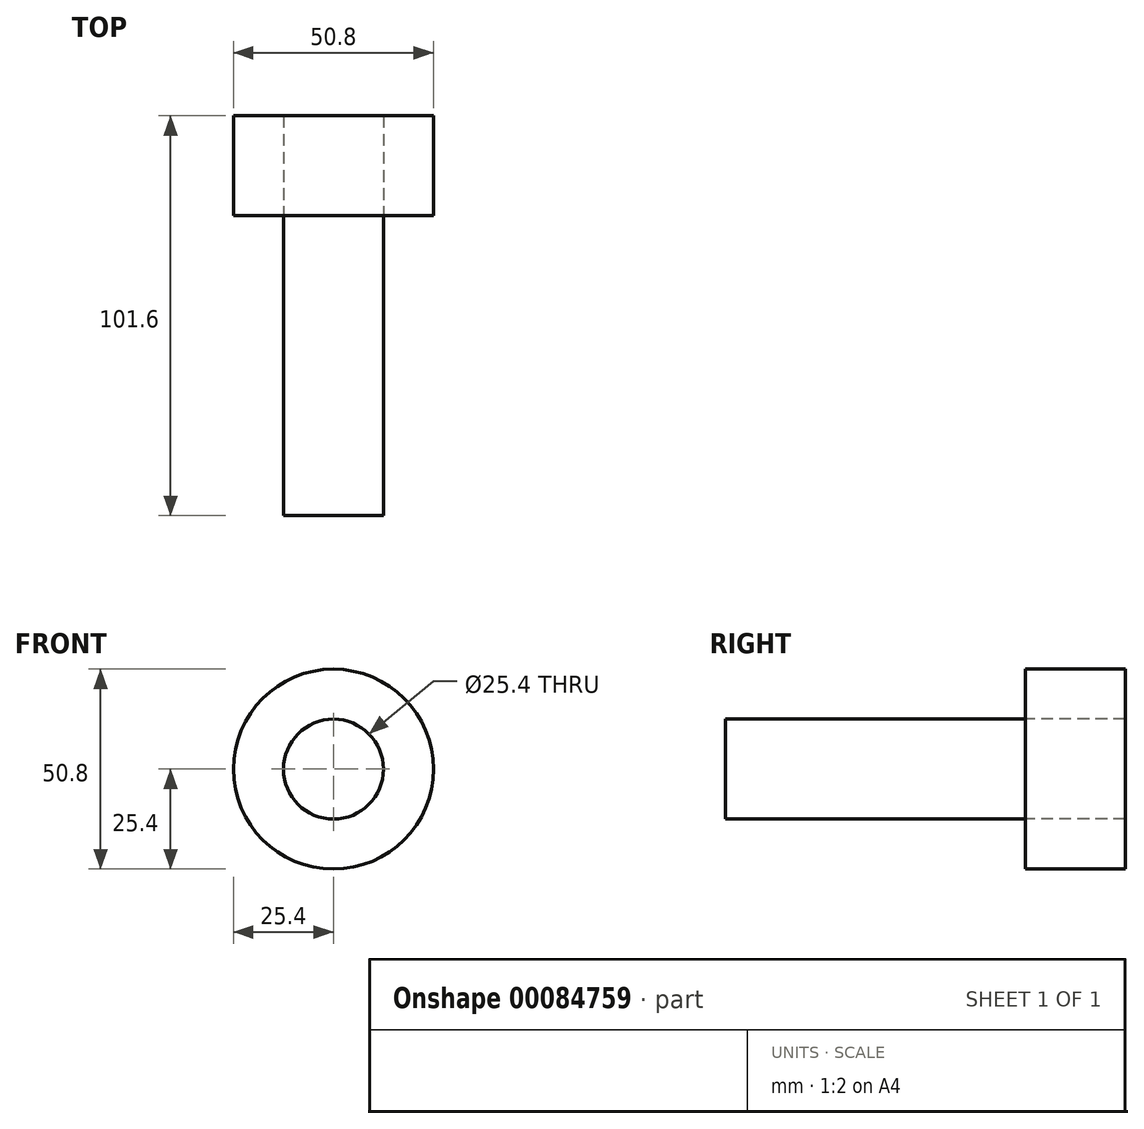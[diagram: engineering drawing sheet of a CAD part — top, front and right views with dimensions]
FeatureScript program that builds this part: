
annotation { "Feature Type Name" : "Feature", "Feature Type Description" : "" }
export const myFeature = defineFeature(function(context is Context, id is Id, definition is map)
    precondition{}
    {
        {
            var Q0;
            Q0=qCreatedBy(makeId("Front.planeOp"),FACE);
            var sketch = newSketch(context, id + "F0", { "sketchPlane" : qUnion([Q0])});
            skCircle(sketch, "E0", {"center": v(0, 0) * mm, "radius": 12.7 * mm});
            skCircle(sketch, "E1", {"center": v(0, 0) * mm, "radius": 25.4 * mm});
            skSolve(sketch);
        }
        {
            var Q0;
            Q0=makeQuery(id+"F0.imprint","IMPRINT",FACE,{"disambiguationData":[TD([[makeQuery(id+"F0.imprint","IMPRINT",EDGE,{"derivedFrom":sQuery(id+"F0.wireOp",EDGE,"E0")}),1.0]])]});
            extrude(context, id + "F1", {"entities" : qUnion([Q0]), "depth" : 76.2 * mm});
        }
        {
            var Q0;
            Q0 = qSketchRegion(id + "F0", true);
            extrude(context, id + "F2", {"entities" : qUnion([Q0]), "operationType" : NewBodyOperationType.ADD, "oppositeDirection" : true, "depth" : 25.4 * mm});
        }
    });
